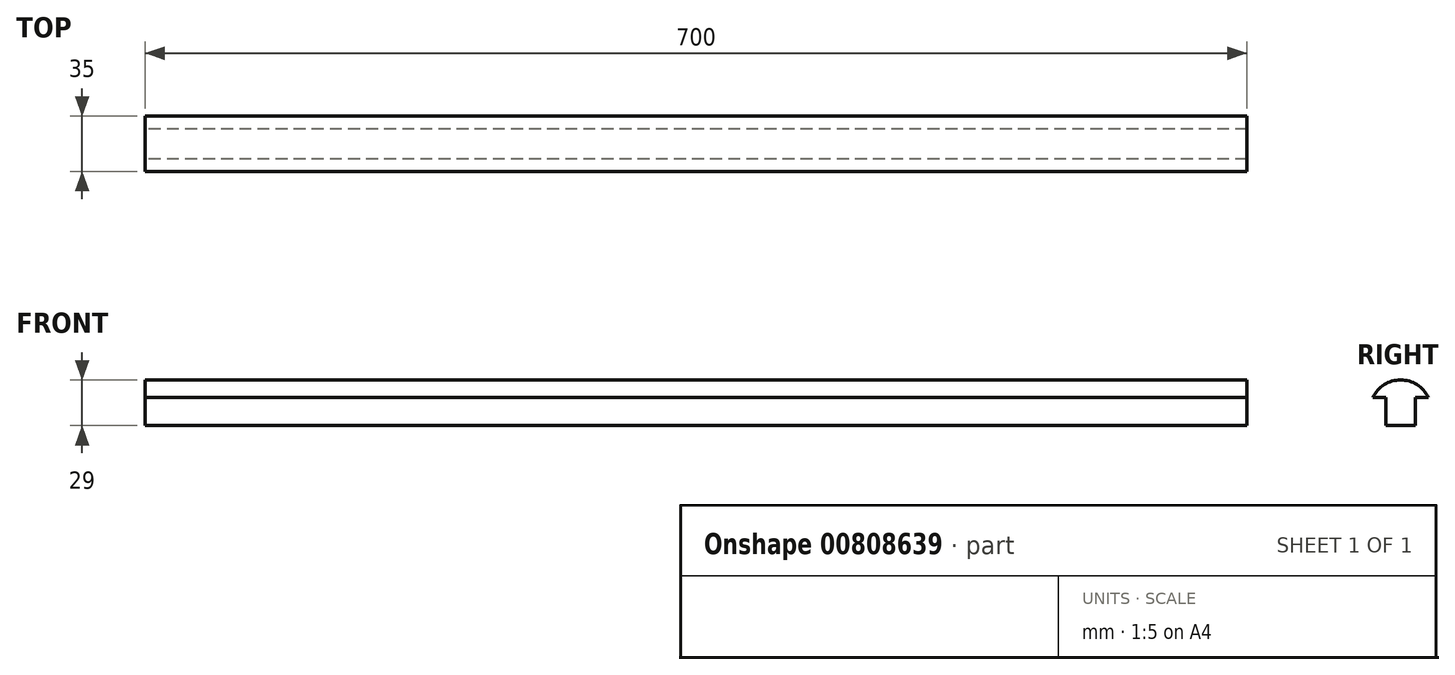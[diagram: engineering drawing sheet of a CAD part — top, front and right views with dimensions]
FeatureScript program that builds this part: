
annotation { "Feature Type Name" : "Feature", "Feature Type Description" : "" }
export const myFeature = defineFeature(function(context is Context, id is Id, definition is map)
    precondition{}
    {
        {
            var Q0;
            Q0=qCreatedBy(makeId("Right.planeOp"),FACE);
            var sketch = newSketch(context, id + "F0", { "sketchPlane" : qUnion([Q0])});
            skLineSegment(sketch, "E0.bottom", {"start": v(9.5, 9) * mm, "end": v(-9.5, 9) * mm});
            skLineSegment(sketch, "E0.top", {"start": v(9.5, -9) * mm, "end": v(-9.5, -9) * mm});
            skLineSegment(sketch, "E0.left", {"start": v(9.5, 9) * mm, "end": v(9.5, -9) * mm});
            skLineSegment(sketch, "E0.right", {"start": v(-9.5, 9) * mm, "end": v(-9.5, -9) * mm});
            skPoint(sketch, "E0.middle", {"position": v(0, 0) * mm});
            skLineSegment(sketch, "E1", {"start": v(9.5, 9) * mm, "end": v(17.5, 9) * mm});
            skLineSegment(sketch, "E2", {"start": v(-9.5, 9) * mm, "end": v(-17.5, 9) * mm});
            skLineSegment(sketch, "E3", {"start": v(0, 9) * mm, "end": v(0, 20) * mm});
            skArc(sketch, "E4", {"start": v(17.5, 9) * mm, "mid": v(0, 20) * mm, "end": v(-17.5, 9) * mm});
            skLineSegment(sketch, "E5", {"start": v(0, 0) * mm, "end": v(0, -9) * mm});
            skSolve(sketch);
        }
        {
            var Q0;
            Q0 = qSketchRegion(id + "F0", true);
            extrude(context, id + "F1", {"entities" : qUnion([Q0]), "endBound" : BoundingType.SYMMETRIC, "depth" : 700 * mm, "offsetDistance" : 25 * mm});
        }
    });
